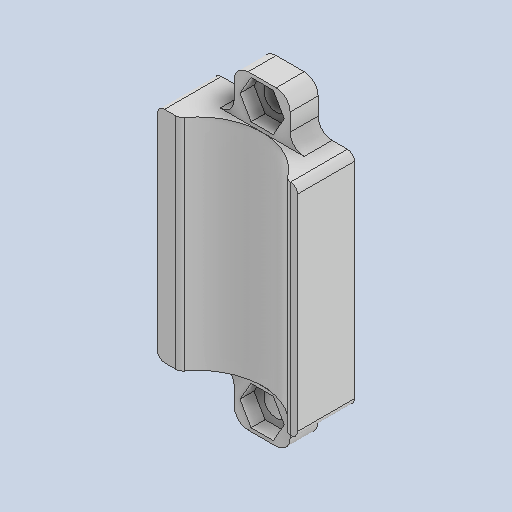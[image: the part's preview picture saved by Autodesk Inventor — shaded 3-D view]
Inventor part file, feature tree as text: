
AUTODESK INVENTOR PART (.ipt)
format: ipt  version: 2023 (Build 270158000, 158)  size: 210,944 bytes
history: native  units: in
note: dims shown in document units (in); Inventor stores cm internally (conversion verified against a paired STEP export)
features: sketch x6, projected_geometry x6, extrude x5, reference x5, other x4, fillet x3, hole x1
ambient origin geometry x8: Origin, YZ Plane, XZ Plane, XY Plane, X Axis, Y Axis, Z Axis, Center Point
bodies: Body1 (feature_tree)
feature tree (30):
  other  "Bryła1"
  sketch  "Szkic1"
  other  "Płaszczyzna konstrukcyjna1"
  extrude  "Wyciągnięcie proste1"  Depth=0.1575in
  extrude  "Wyciągnięcie proste2"  Depth=0.3937in TaperAngle=0.0deg
  extrude  "Wyciągnięcie proste3"  TaperAngle=0.0deg  [1 undecoded]
  hole  "Otwór1"  [1 undecoded]
  extrude  "Wyciągnięcie proste4"  Depth=0.2559in
  extrude  "Wyciągnięcie proste5"  Depth=0.2559in
  fillet  "Zaokrąglenie3"  Radius=0.0787in
  fillet  "Zaokrąglenie4"  Radius=0.2165in
  fillet  "Zaokrąglenie5"  Radius=0.2165in
  reference  "Odniesienie1"
  reference  "Odniesienie2"
  reference  "Odniesienie3"
  reference  "Odniesienie4"
  sketch  "Szkic2"
  reference  "Odniesienie5"
  sketch  "Szkic3"
  projected_geometry  "Pętla rzutowana1"
  sketch  "Szkic4"
  projected_geometry  "Pętla rzutowana2"
  projected_geometry  "Pętla rzutowana3"
  sketch  "Szkic5"
  projected_geometry  "Pętla rzutowana4"
  projected_geometry  "Pętla rzutowana5"
  sketch  "Szkic6"
  projected_geometry  "Pętla rzutowana6"
  other  "<userpath>\Documents\Inventor\generic sumo\generic_3.iam"
  other  "generic_3.iam"
note: 2 required parameter values undecoded (feature->parameter linkage not recoverable at this tier; creation-order binding heuristic only, values carry confidence <= 0.55)
